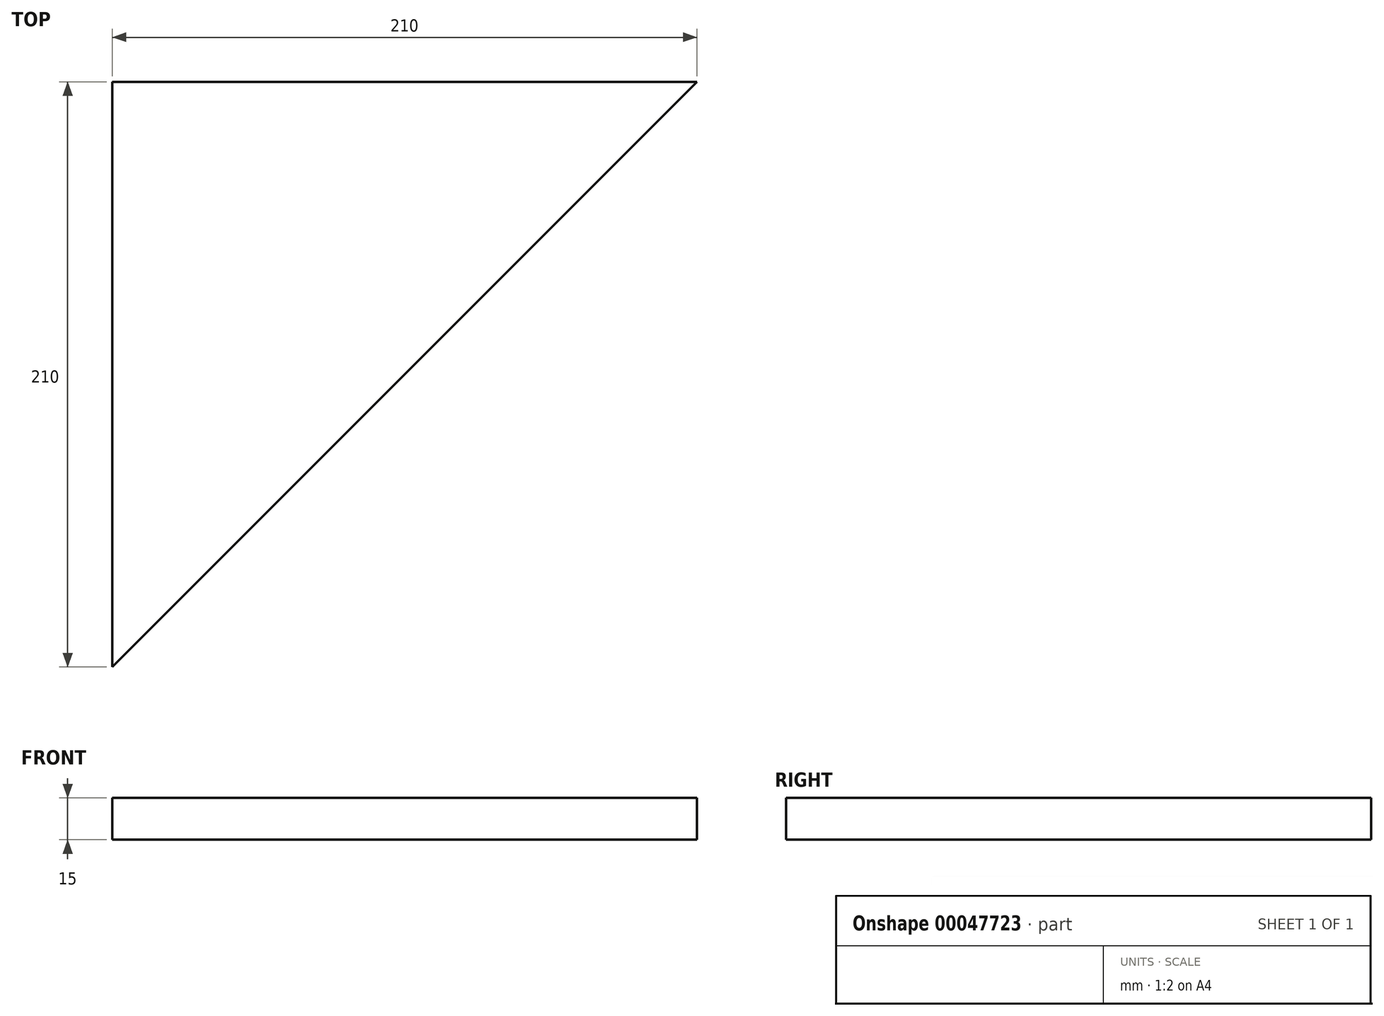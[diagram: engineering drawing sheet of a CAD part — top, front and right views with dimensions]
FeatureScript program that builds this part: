
annotation { "Feature Type Name" : "Feature", "Feature Type Description" : "" }
export const myFeature = defineFeature(function(context is Context, id is Id, definition is map)
    precondition{}
    {
        {
            var Q0;
            Q0=qCreatedBy(makeId("Top.planeOp"),FACE);
            var sketch = newSketch(context, id + "F0", { "sketchPlane" : qUnion([Q0])});
            skLineSegment(sketch, "E0", {"start": v(0, 0) * mm, "end": v(210, 0) * mm});
            skLineSegment(sketch, "E1", {"start": v(0, 0) * mm, "end": v(0, -210) * mm});
            skLineSegment(sketch, "E2", {"start": v(0, -210) * mm, "end": v(210, 0) * mm});
            skSolve(sketch);
        }
        {
            var Q0;
            Q0 = qSketchRegion(id + "F0", true);
            extrude(context, id + "F1", {"entities" : qUnion([Q0]), "depth" : 15 * mm});
        }
    });
